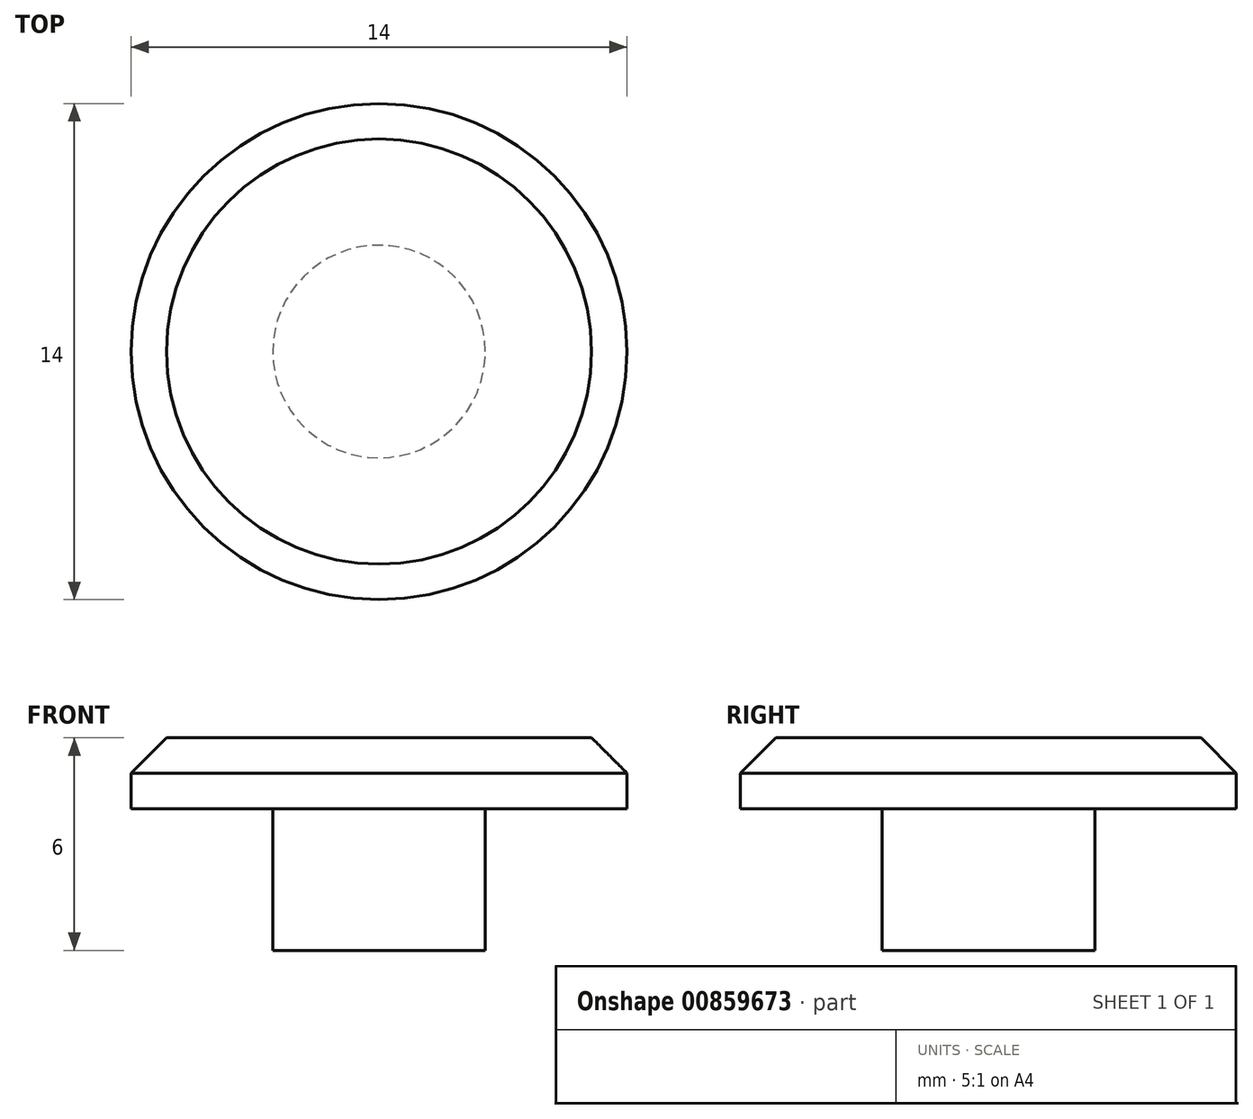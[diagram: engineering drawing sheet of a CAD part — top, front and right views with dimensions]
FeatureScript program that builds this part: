
annotation { "Feature Type Name" : "Feature", "Feature Type Description" : "" }
export const myFeature = defineFeature(function(context is Context, id is Id, definition is map)
    precondition{}
    {
        {
            var Q0;
            Q0=qCreatedBy(makeId("Top.planeOp"),FACE);
            var sketch = newSketch(context, id + "F0", { "sketchPlane" : qUnion([Q0])});
            skCircle(sketch, "E0", {"center": v(0, 0) * mm, "radius": 7 * mm});
            skSolve(sketch);
        }
        {
            var Q0;
            Q0 = qSketchRegion(id + "F0", true);
            extrude(context, id + "F1", {"entities" : qUnion([Q0]), "depth" : 2 * mm, "offsetDistance" : 25 * mm});
        }
        {
            var Q0;
            Q0=makeQuery(id+"F1.opExtrude","CAP_EDGE",EDGE,{"disambiguationData":[OSD([sQuery(id+"F0.wireOp",EDGE,"E0")])],"isStart":false});
            chamfer(context, id + "F2", {"entities" : qUnion([Q0]), "width" : 1 * mm, "tangentPropagation" : true});
        }
        {
            var Q0;
            Q0=makeQuery(id+"F1.opExtrude","CAP_FACE",FACE,{"disambiguationData":[OSD([sQuery(id+"F0.wireOp",EDGE,"E0")])],"isStart":true});
            var sketch = newSketch(context, id + "F3", { "sketchPlane" : qUnion([Q0])});
            skCircle(sketch, "E1", {"center": v(0, 0) * mm, "radius": 3 * mm});
            skSolve(sketch);
        }
        {
            var Q0;
            Q0 = qSketchRegion(id + "F3", true);
            extrude(context, id + "F4", {"entities" : qUnion([Q0]), "operationType" : NewBodyOperationType.ADD, "depth" : 4 * mm, "offsetDistance" : 25 * mm});
        }
    });
